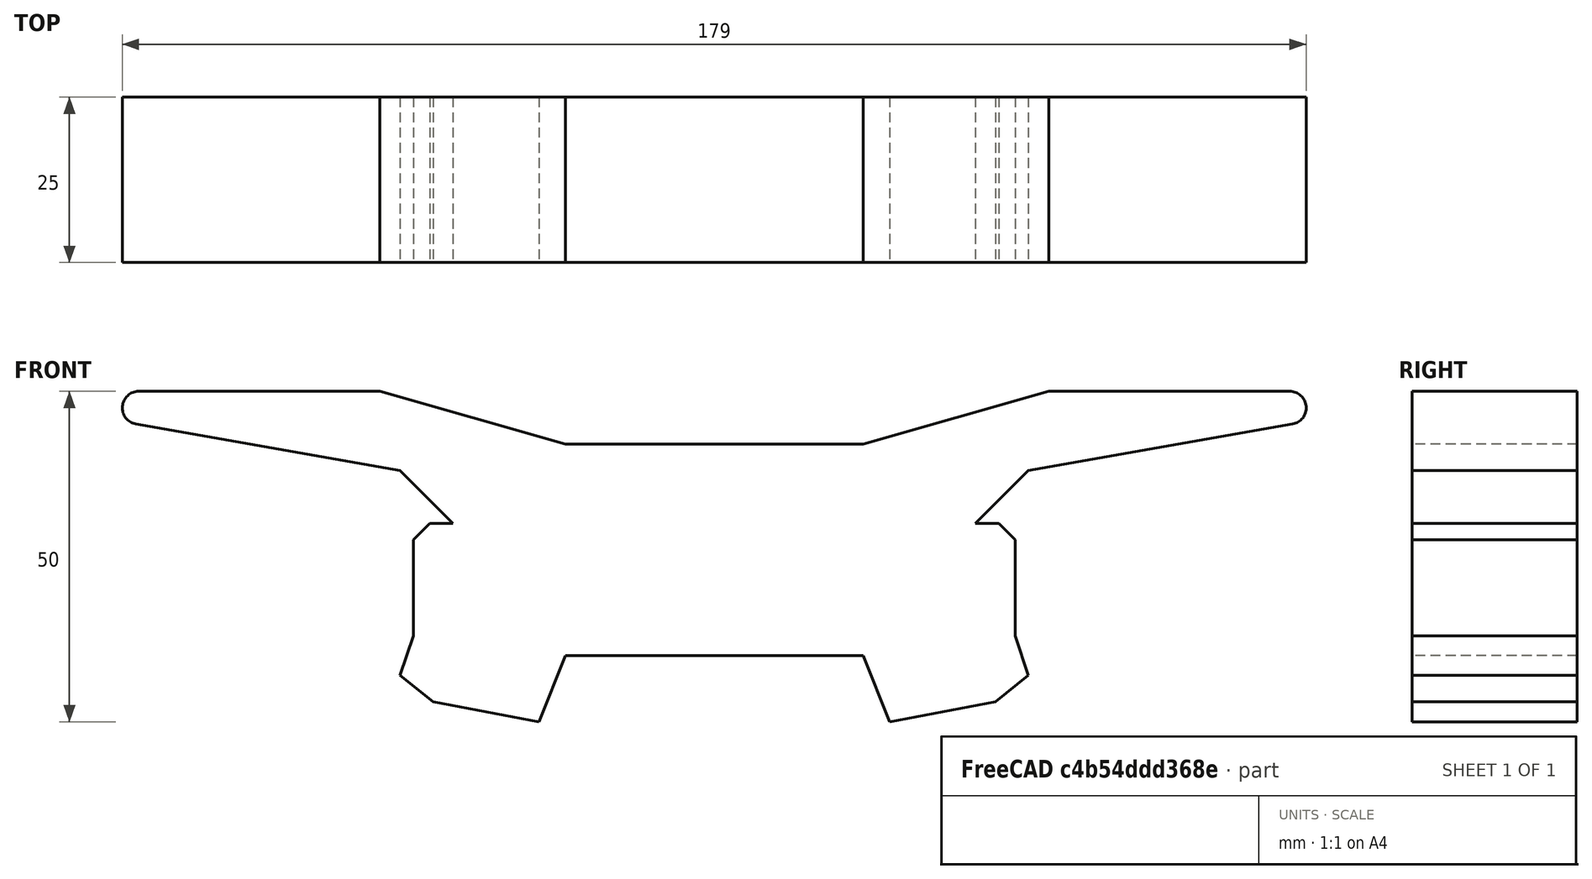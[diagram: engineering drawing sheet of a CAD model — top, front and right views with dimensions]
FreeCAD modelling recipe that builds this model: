
FCSTD DOCUMENT  (FreeCAD 0.18.4R)
Label: part9
License: All rights reserved
LicenseURL: http://en.wikipedia.org/wiki/All_rights_reserved
objects: Sketcher::SketchObject×1, PartDesign::Pad×1, PartDesign::Body×1, App::Part×1
note: 4 computed .brp shape members not serialized (recipe doc carries the construction recipe); baked Part::Feature solids carry a one-line shape summary decoded from their .brp

FEATURE [Sketcher::SketchObject] Sketch003  label="Sketch"
  MapMode = 5
  Placement = pos=(0,0,0) rot=(1,0,0;1.5708rad)
  Support = -> [XZ_Plane003]
  sketch-geometry (26):
    g0: LineSegment StartX=-22.5 StartY=59.5 StartZ=0 EndX=22.5 EndY=59.5 EndZ=0
    g1: LineSegment StartX=22.5 StartY=59.5 StartZ=0 EndX=50.5966 EndY=67.5 EndZ=0
    g2: LineSegment StartX=50.5966 StartY=67.5 StartZ=0 EndX=87 EndY=67.5 EndZ=0
    g3: ArcOfCircle CenterX=87 CenterY=65 CenterZ=0 NormalX=0 NormalY=0 NormalZ=1 AngleXU=0 Radius=2.5 StartAngle=4.88684 EndAngle=7.85398
    g4: LineSegment StartX=87.4339 StartY=62.5379 StartZ=0 EndX=47.5 EndY=55.5 EndZ=0
    g5: LineSegment StartX=47.5 StartY=55.5 StartZ=0 EndX=39.5 EndY=47.5 EndZ=0
    g6: LineSegment StartX=39.5 StartY=47.5 StartZ=0 EndX=43.0147 EndY=47.5 EndZ=0
    g7: LineSegment StartX=43.0147 StartY=47.5 StartZ=0 EndX=45.5 EndY=45.0147 EndZ=0
    g8: LineSegment StartX=45.5 StartY=45.0147 StartZ=0 EndX=45.5 EndY=30.5 EndZ=0
    g9: LineSegment StartX=45.5 StartY=30.5 StartZ=0 EndX=47.5 EndY=24.5 EndZ=0
    g10: LineSegment StartX=47.5 StartY=24.5 StartZ=0 EndX=42.5 EndY=20.5 EndZ=0
    g11: LineSegment StartX=42.5 StartY=20.5 StartZ=0 EndX=26.5 EndY=17.5 EndZ=0
    g12: LineSegment StartX=26.5 StartY=17.5 StartZ=0 EndX=22.5 EndY=27.5 EndZ=0
    g13: LineSegment StartX=-22.5 StartY=27.5 StartZ=0 EndX=-26.5 EndY=17.5 EndZ=0
    g14: LineSegment StartX=-26.5 StartY=17.5 StartZ=0 EndX=-42.5 EndY=20.5 EndZ=0
    g15: LineSegment StartX=-42.5 StartY=20.5 StartZ=0 EndX=-47.5 EndY=24.5 EndZ=0
    g16: LineSegment StartX=-47.5 StartY=24.5 StartZ=0 EndX=-45.5 EndY=30.5 EndZ=0
    g17: LineSegment StartX=-45.5 StartY=30.5 StartZ=0 EndX=-45.5 EndY=45.0147 EndZ=0
    g18: LineSegment StartX=-45.5 StartY=45.0147 StartZ=0 EndX=-43.0147 EndY=47.5 EndZ=0
    g19: LineSegment StartX=-43.0147 StartY=47.5 StartZ=0 EndX=-39.5 EndY=47.5 EndZ=0
    g20: LineSegment StartX=-39.5 StartY=47.5 StartZ=0 EndX=-47.5 EndY=55.5 EndZ=0
    g21: LineSegment StartX=-47.5 StartY=55.5 StartZ=0 EndX=-87.4339 EndY=62.5379 EndZ=0
    g22: ArcOfCircle CenterX=-87 CenterY=65 CenterZ=0 NormalX=0 NormalY=0 NormalZ=1 AngleXU=0 Radius=2.5 StartAngle=1.5708 EndAngle=4.53794
    g23: LineSegment StartX=-87 StartY=67.5 StartZ=0 EndX=-50.5966 EndY=67.5 EndZ=0
    g24: LineSegment StartX=-50.5966 StartY=67.5 StartZ=0 EndX=-22.5 EndY=59.5 EndZ=0
    g25: LineSegment StartX=-22.5 StartY=27.5 StartZ=0 EndX=22.5 EndY=27.5 EndZ=0
  constraints (66):
    c: Coincident(g0,g1)
    c: Coincident(g1,g2)
    c: Coincident(g3,g2)
    c: Coincident(g4,g5)
    c: Coincident(g5,g6)
    c: Coincident(g6,g7)
    c: Coincident(g7,g8)
    c: Vertical(g8)
    c: Coincident(g8,g9)
    c: Coincident(g9,g10)
    c: Coincident(g10,g11)
    c: Coincident(g11,g12)
    c: Coincident(g13,g14)
    c: Coincident(g14,g15)
    c: Coincident(g15,g16)
    c: Coincident(g16,g17)
    c: Coincident(g17,g18)
    c: Coincident(g18,g19)
    c: Coincident(g19,g20)
    c: Coincident(g20,g21)
    c: Coincident(g22,g21)
    c: Coincident(g23,g24)
    c: Coincident(g24,g0)
    c: Symmetric(g0,g0,g-2)
    c: Symmetric(g23,g1,g-2)
    c: Symmetric(g22,g2,g-2)
    c: Symmetric(g21,g3,g-2)
    c: Coincident(g22,g23)
    c: Coincident(g4,g3)
    c: Symmetric(g20,g4,g-2)
    c: Symmetric(g19,g5,g-2)
    c: Symmetric(g18,g6,g-2)
    c: Symmetric(g17,g7,g-2)
    c: Symmetric(g16,g8,g-2)
    c: Symmetric(g15,g9,g-2)
    c: Symmetric(g14,g10,g-2)
    c: Symmetric(g13,g11,g-2)
    c: Symmetric(g13,g12,g-2)
    c: Tangent(g22,g23)
    c: Tangent(g2,g3)
    c: Tangent(g4,g3)
    c: Horizontal(g23)
    c: DistanceX(g22,g3) = 174
    c: DistanceY(g0,g23) = 8
    c: DistanceX(g0,g0) = 45
    c: Radius(g22) = 2.5
    c: DistanceY(g20,g0) = 4
    c: Horizontal(g19)
    c: DistanceX(g13,g12) = 45
    c: DistanceX(g16,g13) = 23
    c: DistanceX(g19,g13) = 17
    c: Angle(g17,g18) = 2.35619
    c: DistanceY(g13,g0) = 32
    c: Angle(g20,g19) = 0.785398
    c: DistanceY(g13,g13) = 10
    c: DistanceX(g13,g13) = 4
    c: DistanceX(g14,g13) = 20
    c: DistanceY(g14,g13) = 7
    c: DistanceX(g15,g13) = 25
    c: DistanceY(g15,g13) = 3
    c: DistanceY(g13,g16) = 3
    c: DistanceY(g13,g19) = 20
    c: Equal(g18,g19)
    c: Coincident(g25,g13)
    c: Coincident(g25,g12)
    c: DistanceY(g-1,g0) = 59.5
FEATURE [PartDesign::Pad] Pad002  label="Pad"
  Length = 25
  Length2 = 100
  Midplane = true
  Placement = pos=(0,0,0) rot=(1,0,0;1.5708rad)
  Profile = -> Sketch003
  Type = 0
FEATURE [PartDesign::Body] Body001  label="Body"
  Group = -> [Sketch003,Pad002]
  Origin = -> Origin003
  Tip = -> Pad002
FEATURE [App::Part] Part001  label="part9"
  Group = -> [Body001]
  Origin = -> Origin001
